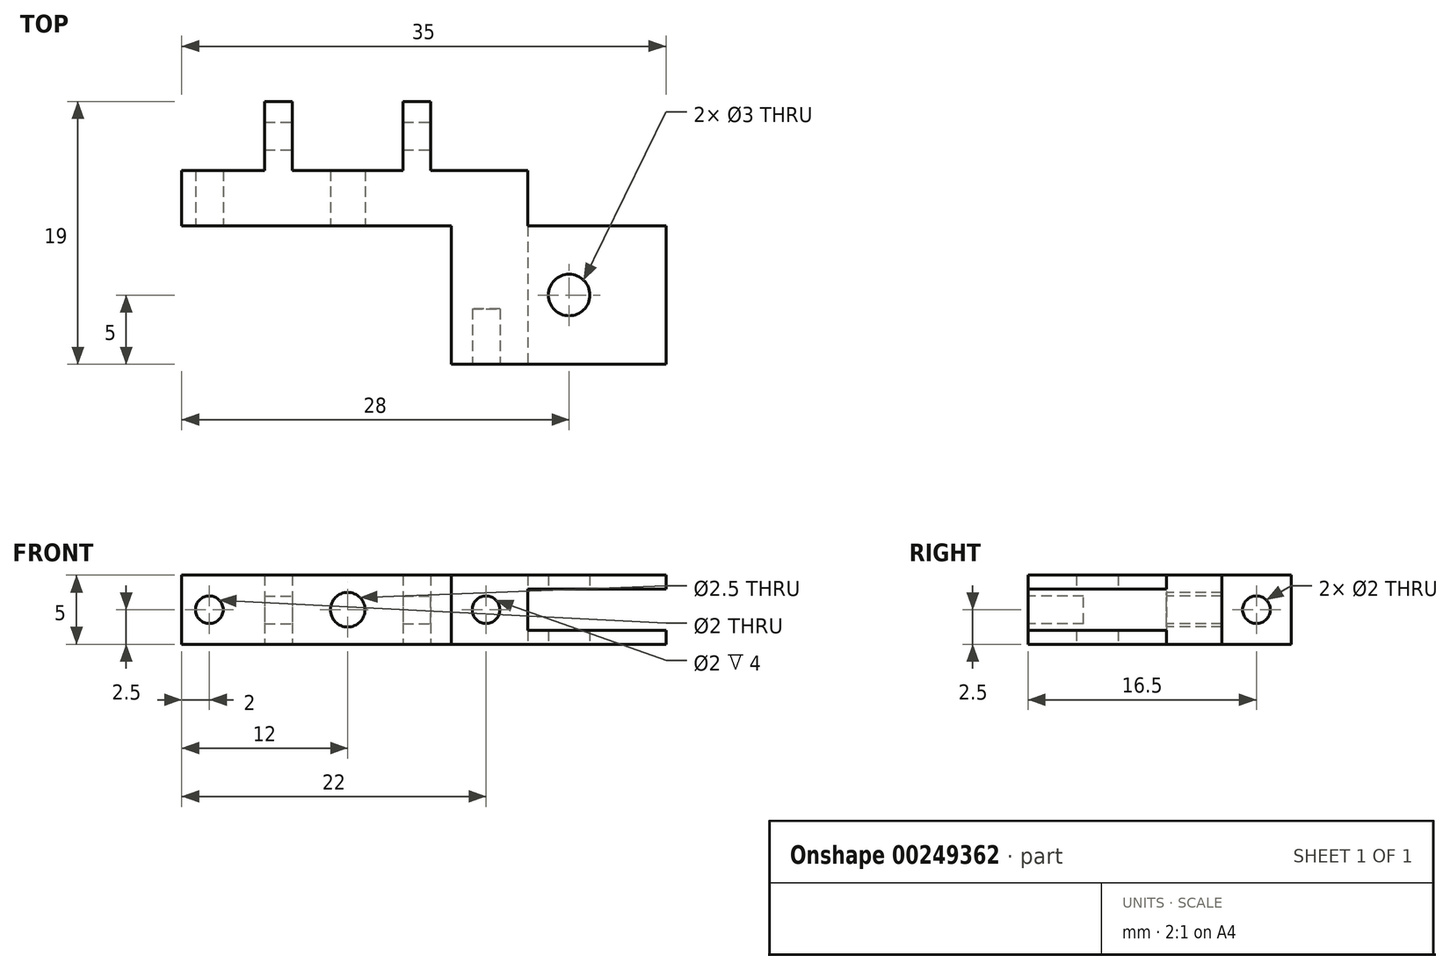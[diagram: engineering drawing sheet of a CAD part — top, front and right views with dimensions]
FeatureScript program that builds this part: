
annotation { "Feature Type Name" : "Feature", "Feature Type Description" : "" }
export const myFeature = defineFeature(function(context is Context, id is Id, definition is map)
    precondition{}
    {
        {
            var Q0;
            Q0=qCreatedBy(makeId("Top.planeOp"),FACE);
            var sketch = newSketch(context, id + "F0", { "sketchPlane" : qUnion([Q0])});
            skLineSegment(sketch, "E0", {"start": v(23, 5) * mm, "end": v(23, -5) * mm});
            skLineSegment(sketch, "E1", {"start": v(23, -5) * mm, "end": v(7.5, -5) * mm});
            skLineSegment(sketch, "E2", {"start": v(7.5, -5) * mm, "end": v(7.5, 5) * mm});
            skLineSegment(sketch, "E3", {"start": v(7.5, 5) * mm, "end": v(-12, 5) * mm});
            skLineSegment(sketch, "E4", {"start": v(-12, 5) * mm, "end": v(-12, 9) * mm});
            skLineSegment(sketch, "E5", {"start": v(-12, 9) * mm, "end": v(13, 9) * mm});
            skLineSegment(sketch, "E6", {"start": v(13, 9) * mm, "end": v(13, 5) * mm});
            skLineSegment(sketch, "E7", {"start": v(13, 5) * mm, "end": v(23, 5) * mm});
            skCircle(sketch, "E8", {"center": v(16, 0) * mm, "radius": 1.5 * mm});
            skLineSegment(sketch, "E9.bottom", {"start": v(-4, 9) * mm, "end": v(-6, 9) * mm});
            skLineSegment(sketch, "E9.top", {"start": v(-4, 14) * mm, "end": v(-6, 14) * mm});
            skLineSegment(sketch, "E9.left", {"start": v(-4, 9) * mm, "end": v(-4, 14) * mm});
            skLineSegment(sketch, "E9.right", {"start": v(-6, 9) * mm, "end": v(-6, 14) * mm});
            skLineSegment(sketch, "E10.MirrorCS", {"start": v(4, 9) * mm, "end": v(4, 14) * mm});
            skLineSegment(sketch, "E11.MirrorCS", {"start": v(4, 9) * mm, "end": v(6, 9) * mm});
            skLineSegment(sketch, "E12.MirrorCS", {"start": v(4, 14) * mm, "end": v(6, 14) * mm});
            skLineSegment(sketch, "E13.MirrorCS", {"start": v(6, 9) * mm, "end": v(6, 14) * mm});
            skSolve(sketch);
        }
        {
            var Q0;
            Q0 = qSketchRegion(id + "F0", true);
            extrude(context, id + "F1", {"entities" : qUnion([Q0]), "endBound" : BoundingType.SYMMETRIC, "depth" : 5 * mm});
        }
        {
            var Q0;
            Q0=makeQuery(id+"F1.opExtrude","SWEPT_FACE",FACE,{"disambiguationData":[OSD([sQuery(id+"F0.wireOp",EDGE,"E3")])]});
            var sketch = newSketch(context, id + "F2", { "sketchPlane" : qUnion([Q0])});
            skCircle(sketch, "E14", {"center": v(0, 0) * mm, "radius": 1.25 * mm});
            skCircle(sketch, "E15", {"center": v(-10, 0) * mm, "radius": 1 * mm});
            skSolve(sketch);
        }
        {
            var Q0;
            Q0 = qSketchRegion(id + "F2", true);
            extrude(context, id + "F3", {"entities" : qUnion([Q0]), "operationType" : NewBodyOperationType.REMOVE, "endBound" : BoundingType.THROUGH_ALL, "oppositeDirection" : true, "depth" : 40 * mm});
        }
        {
            var Q0;
            Q0=makeQuery(id+"F1.opExtrude","SWEPT_FACE",FACE,{"disambiguationData":[OSD([sQuery(id+"F0.wireOp",EDGE,"E1")])]});
            var sketch = newSketch(context, id + "F4", { "sketchPlane" : qUnion([Q0])});
            skLineSegment(sketch, "E16.bottom", {"start": v(23, -1.5) * mm, "end": v(13, -1.5) * mm});
            skLineSegment(sketch, "E16.top", {"start": v(23, 1.5) * mm, "end": v(13, 1.5) * mm});
            skLineSegment(sketch, "E16.left", {"start": v(23, -1.5) * mm, "end": v(23, 1.5) * mm});
            skLineSegment(sketch, "E16.right", {"start": v(13, -1.5) * mm, "end": v(13, 1.5) * mm});
            skPoint(sketch, "E16.middle", {"position": v(18, 0) * mm});
            skSolve(sketch);
        }
        {
            var Q0;
            Q0 = qSketchRegion(id + "F4", true);
            extrude(context, id + "F5", {"entities" : qUnion([Q0]), "operationType" : NewBodyOperationType.REMOVE, "endBound" : BoundingType.THROUGH_ALL, "oppositeDirection" : true, "depth" : 25 * mm});
        }
        {
            var Q0;
            Q0=makeQuery(id+"F1.opExtrude","SWEPT_FACE",FACE,{"disambiguationData":[OSD([sQuery(id+"F0.wireOp",EDGE,"E1")])]});
            var sketch = newSketch(context, id + "F6", { "sketchPlane" : qUnion([Q0])});
            skCircle(sketch, "E17", {"center": v(10, 0) * mm, "radius": 1 * mm});
            skSolve(sketch);
        }
        {
            var Q0;
            Q0 = qSketchRegion(id + "F6", true);
            extrude(context, id + "F7", {"entities" : qUnion([Q0]), "operationType" : NewBodyOperationType.REMOVE, "oppositeDirection" : true, "depth" : 4 * mm});
        }
        {
            var Q0;
            Q0=makeQuery(id+"F1.opExtrude","SWEPT_FACE",FACE,{"disambiguationData":[OSD([sQuery(id+"F0.wireOp",EDGE,"E13.MirrorCS")])]});
            var sketch = newSketch(context, id + "F8", { "sketchPlane" : qUnion([Q0])});
            skCircle(sketch, "E18", {"center": v(11.5, 0) * mm, "radius": 1 * mm});
            skSolve(sketch);
        }
        {
            var Q0;
            Q0 = qSketchRegion(id + "F8", true);
            extrude(context, id + "F9", {"entities" : qUnion([Q0]), "operationType" : NewBodyOperationType.REMOVE, "endBound" : BoundingType.THROUGH_ALL, "oppositeDirection" : true, "depth" : 25 * mm});
        }
    });
